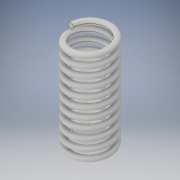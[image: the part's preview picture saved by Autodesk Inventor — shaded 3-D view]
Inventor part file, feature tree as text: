
AUTODESK INVENTOR PART (.ipt)
format: ipt  version: 2018 (Build 220112000, 112)  size: 629,248 bytes
history: native  units: in
note: dims shown in document units (in); Inventor stores cm internally (conversion verified against a paired STEP export)
features: helix x1, sketch x1
ambient origin geometry x8: Origin, YZ Plane, XZ Plane, XY Plane, X Axis, Y Axis, Z Axis, Center Point
bodies: Solid1 (feature_tree)
feature tree (2):
  helix  "Coil1"  [1 undecoded]
  sketch  "Sketch1"  dims[d1=0.16in d2=1.0in d3=0.6695in d4=3.937in d5=0.0in d6=90.0deg d7=90.0deg d8=90.0deg d9=90.0deg]
note: 1 required parameter value undecoded (feature->parameter linkage not recoverable at this tier; creation-order binding heuristic only, values carry confidence <= 0.55)
